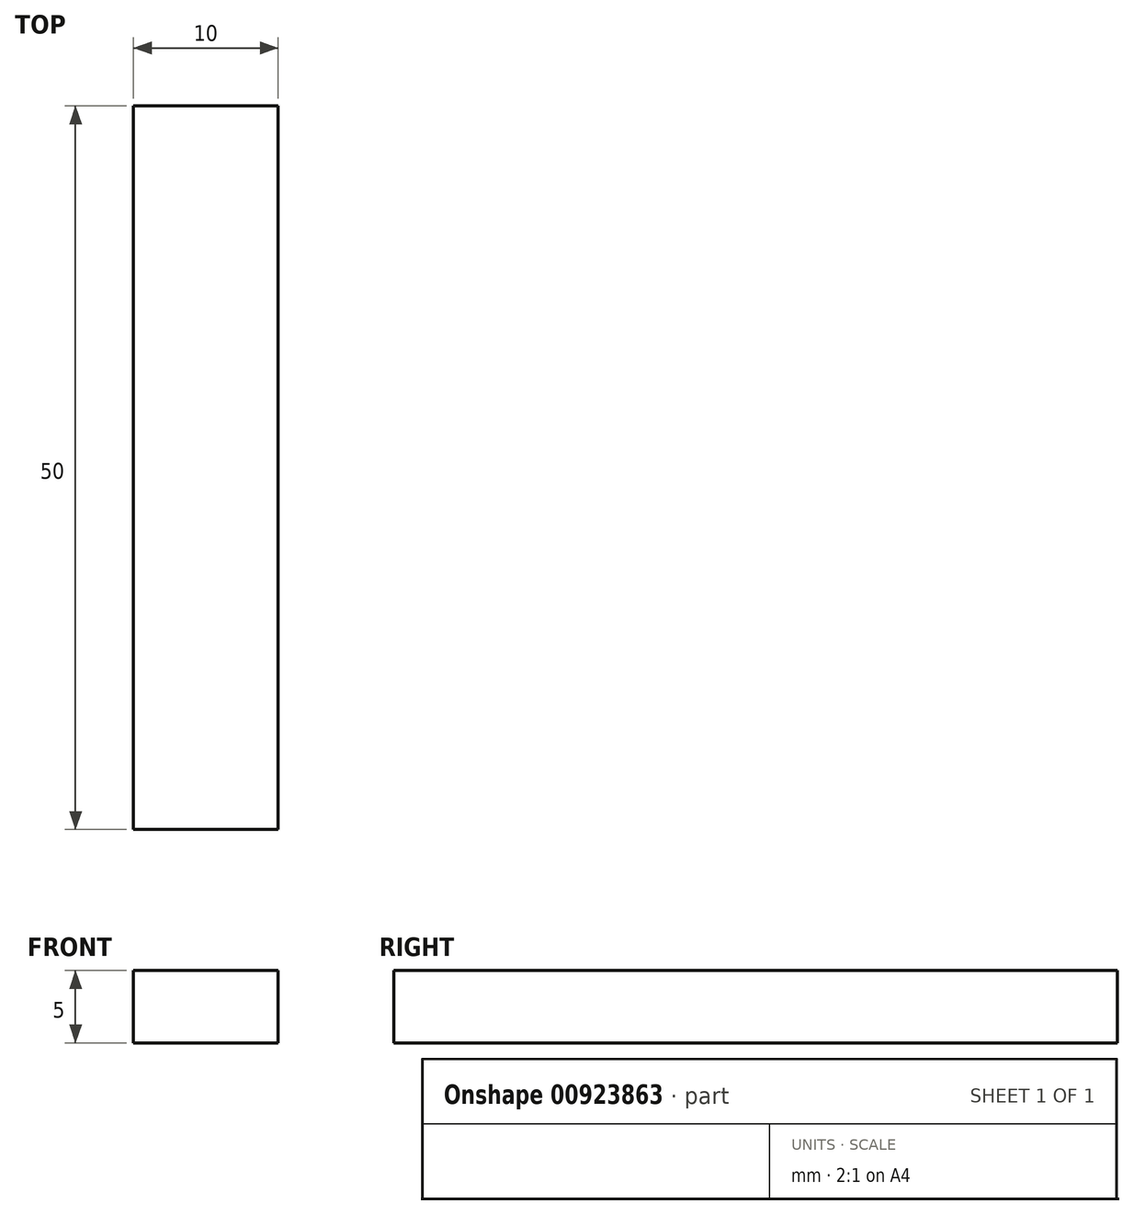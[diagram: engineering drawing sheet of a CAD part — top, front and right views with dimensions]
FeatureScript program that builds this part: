
annotation { "Feature Type Name" : "Feature", "Feature Type Description" : "" }
export const myFeature = defineFeature(function(context is Context, id is Id, definition is map)
    precondition{}
    {
        {
            var Q0;
            Q0=qCreatedBy(makeId("Front.planeOp"),FACE);
            var sketch = newSketch(context, id + "F0", { "sketchPlane" : qUnion([Q0])});
            skLineSegment(sketch, "E0.bottom", {"start": v(5, -2.5) * mm, "end": v(-5, -2.5) * mm});
            skLineSegment(sketch, "E0.top", {"start": v(5, 2.5) * mm, "end": v(-5, 2.5) * mm});
            skLineSegment(sketch, "E0.left", {"start": v(5, -2.5) * mm, "end": v(5, 2.5) * mm});
            skLineSegment(sketch, "E0.right", {"start": v(-5, -2.5) * mm, "end": v(-5, 2.5) * mm});
            skPoint(sketch, "E0.middle", {"position": v(0, 0) * mm});
            skSolve(sketch);
        }
        {
            var Q0;
            Q0 = qSketchRegion(id + "F0", true);
            extrude(context, id + "F1", {"entities" : qUnion([Q0]), "depth" : 50 * mm, "offsetDistance" : 25 * mm});
        }
    });
